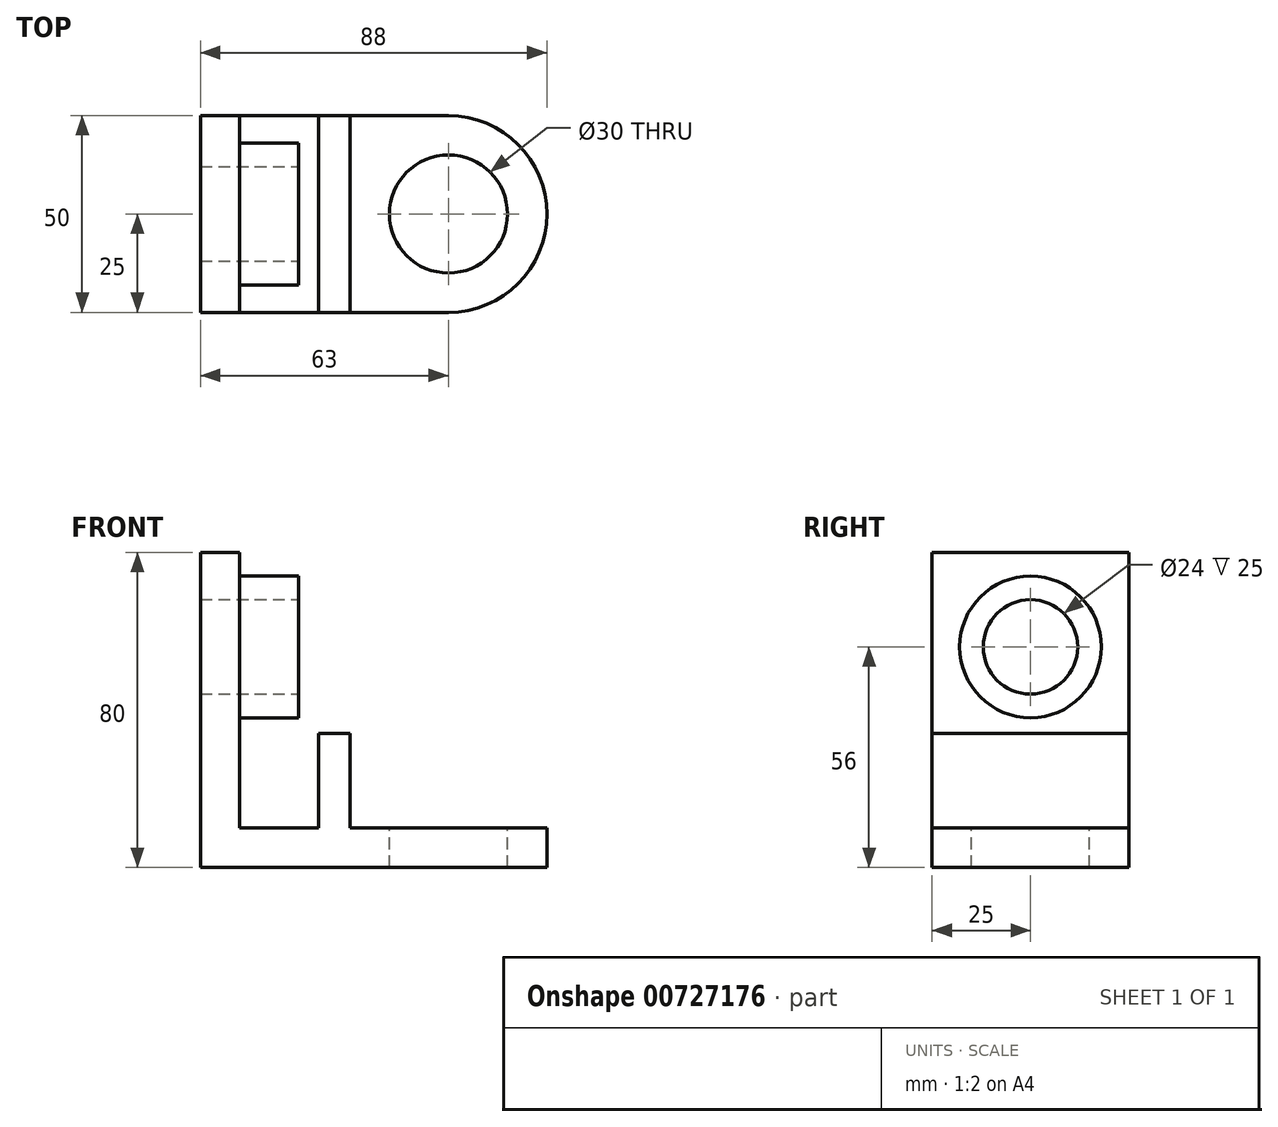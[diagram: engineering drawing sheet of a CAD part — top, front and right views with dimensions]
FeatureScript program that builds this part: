
annotation { "Feature Type Name" : "Feature", "Feature Type Description" : "" }
export const myFeature = defineFeature(function(context is Context, id is Id, definition is map)
    precondition{}
    {
        {
            var Q0;
            Q0=qCreatedBy(makeId("Front.planeOp"),FACE);
            var sketch = newSketch(context, id + "F0", { "sketchPlane" : qUnion([Q0])});
            skLineSegment(sketch, "E0", {"start": v(0, 0) * mm, "end": v(0, 80) * mm});
            skLineSegment(sketch, "E1", {"start": v(0, 80) * mm, "end": v(10, 80) * mm});
            skLineSegment(sketch, "E2", {"start": v(10, 80) * mm, "end": v(10, 10) * mm});
            skLineSegment(sketch, "E3", {"start": v(10, 10) * mm, "end": v(30, 10) * mm});
            skLineSegment(sketch, "E4", {"start": v(30, 10) * mm, "end": v(30, 34) * mm});
            skLineSegment(sketch, "E5", {"start": v(30, 34) * mm, "end": v(38, 34) * mm});
            skLineSegment(sketch, "E6", {"start": v(38, 34) * mm, "end": v(38, 10) * mm});
            skLineSegment(sketch, "E7", {"start": v(38, 10) * mm, "end": v(88, 10) * mm});
            skLineSegment(sketch, "E8", {"start": v(88, 10) * mm, "end": v(88, 0) * mm});
            skLineSegment(sketch, "E9", {"start": v(88, 0) * mm, "end": v(0, 0) * mm});
            skSolve(sketch);
        }
        {
            var Q0;
            Q0 = qSketchRegion(id + "F0", true);
            extrude(context, id + "F1", {"entities" : qUnion([Q0]), "depth" : 50 * mm, "offsetDistance" : 25 * mm});
        }
        {
            var Q0;
            Q0=makeQuery(id+"F1.opExtrude","CAP_EDGE",EDGE,{"disambiguationData":[OSD([sQuery(id+"F0.wireOp",EDGE,"E8")])],"isStart":false});
            fillet(context, id + "F2", {"entities" : qUnion([Q0]), "radius" : 25 * mm, "tangentPropagation" : true, "allowEdgeOverflow" : false});
        }
        {
            var Q0;
            Q0=makeQuery(id+"F1.opExtrude","CAP_EDGE",EDGE,{"disambiguationData":[OSD([sQuery(id+"F0.wireOp",EDGE,"E8")])],"isStart":true});
            fillet(context, id + "F3", {"entities" : qUnion([Q0]), "radius" : 25 * mm, "tangentPropagation" : true, "allowEdgeOverflow" : false});
        }
        {
            var Q0;
            Q0=makeQuery(id+"F1.opExtrude","SWEPT_FACE",FACE,{"disambiguationData":[OSD([sQuery(id+"F0.wireOp",EDGE,"E7")])]});
            var sketch = newSketch(context, id + "F4", { "sketchPlane" : qUnion([Q0])});
            skCircle(sketch, "E10", {"center": v(63, -25) * mm, "radius": 15 * mm});
            skSolve(sketch);
        }
        {
            var Q0;
            Q0 = qSketchRegion(id + "F4", true);
            extrude(context, id + "F5", {"entities" : qUnion([Q0]), "operationType" : NewBodyOperationType.REMOVE, "endBound" : BoundingType.UP_TO_NEXT, "oppositeDirection" : true, "depth" : 25 * mm, "offsetDistance" : 25 * mm});
        }
        {
            var Q0;
            Q0=makeQuery(id+"F1.opExtrude","SWEPT_FACE",FACE,{"disambiguationData":[OSD([sQuery(id+"F0.wireOp",EDGE,"E2")])]});
            var sketch = newSketch(context, id + "F6", { "sketchPlane" : qUnion([Q0])});
            skLineSegment(sketch, "E11", {"start": v(0, 0) * mm, "end": v(0, 56) * mm});
            skCircle(sketch, "E12", {"center": v(-25, 56) * mm, "radius": 18 * mm});
            skSolve(sketch);
        }
        {
            var Q0;
            Q0 = qSketchRegion(id + "F6", true);
            extrude(context, id + "F7", {"entities" : qUnion([Q0]), "operationType" : NewBodyOperationType.ADD, "depth" : 15 * mm, "offsetDistance" : 25 * mm});
        }
        {
            var Q0;
            Q0=makeQuery(id+"F7.opExtrude","CAP_FACE",FACE,{"disambiguationData":[OSD([sQuery(id+"F6.wireOp",EDGE,"E12")])],"isStart":false});
            var sketch = newSketch(context, id + "F8", { "sketchPlane" : qUnion([Q0])});
            skCircle(sketch, "E13", {"center": v(-25, 56) * mm, "radius": 12 * mm});
            skSolve(sketch);
        }
        {
            var Q0;
            Q0 = qSketchRegion(id + "F8", true);
            extrude(context, id + "F9", {"entities" : qUnion([Q0]), "operationType" : NewBodyOperationType.REMOVE, "endBound" : BoundingType.UP_TO_NEXT, "oppositeDirection" : true, "depth" : 25 * mm, "offsetDistance" : 25 * mm});
        }
    });
